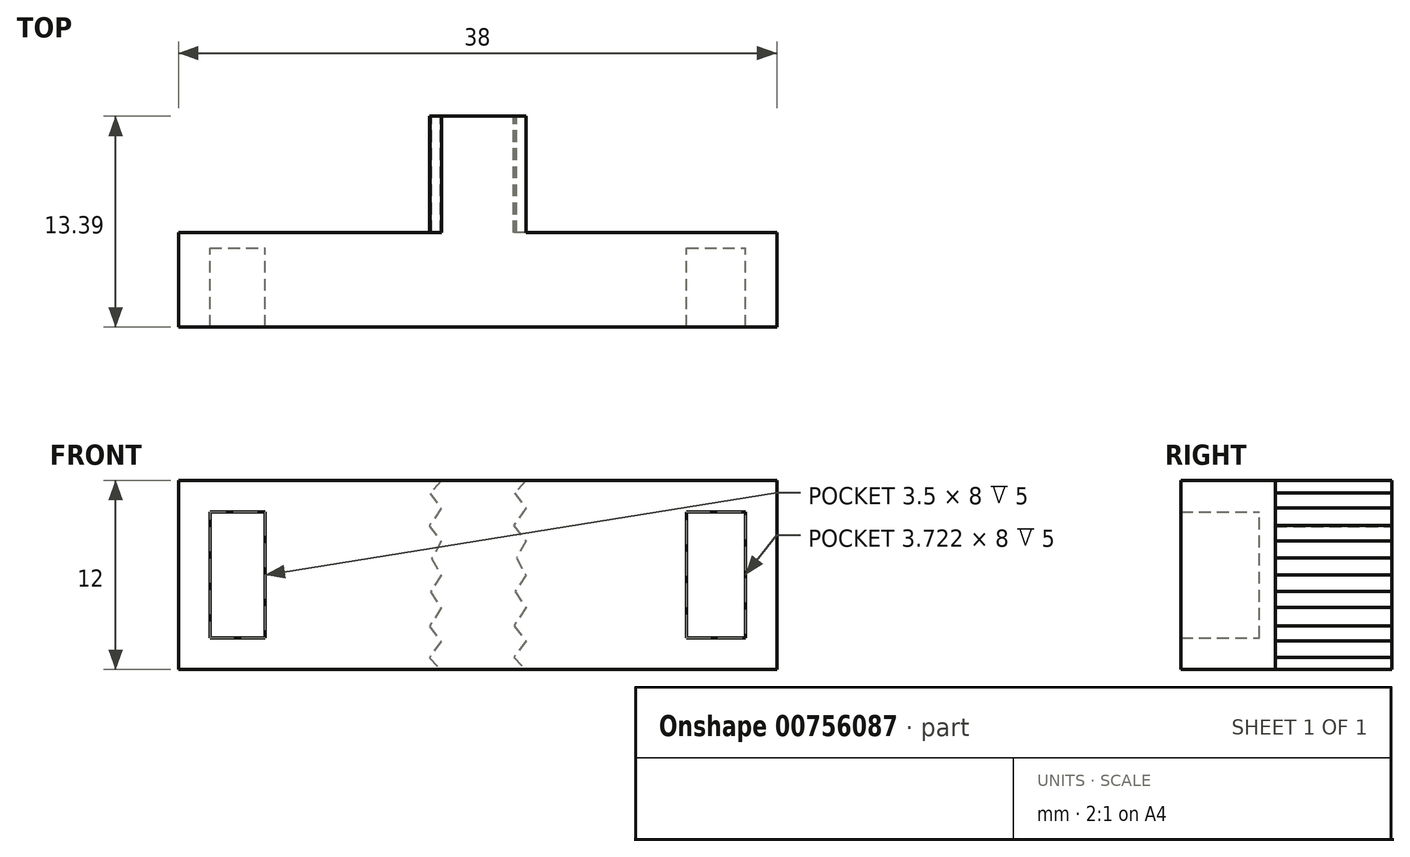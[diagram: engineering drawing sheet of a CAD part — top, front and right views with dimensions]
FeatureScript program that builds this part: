
annotation { "Feature Type Name" : "Feature", "Feature Type Description" : "" }
export const myFeature = defineFeature(function(context is Context, id is Id, definition is map)
    precondition{}
    {
        {
            var Q0;
            Q0=qCreatedBy(makeId("Front.planeOp"),FACE);
            var sketch = newSketch(context, id + "F0", { "sketchPlane" : qUnion([Q0])});
            skLineSegment(sketch, "E0", {"start": v(-23.24, 11.53) * mm, "end": v(10.76, 11.53) * mm});
            skLineSegment(sketch, "E1", {"start": v(-19.74, 17.19) * mm, "end": v(-19.74, 19.53) * mm});
            skLineSegment(sketch, "E2", {"start": v(-19.74, 19.53) * mm, "end": v(7.03, 19.53) * mm});
            skLineSegment(sketch, "E3", {"start": v(7.03, 19.53) * mm, "end": v(7.03, 13.6) * mm});
            skLineSegment(sketch, "E4.bottom", {"start": v(-23.24, 11.53) * mm, "end": v(-19.74, 11.53) * mm});
            skLineSegment(sketch, "E4.top", {"start": v(-23.24, 19.53) * mm, "end": v(-19.74, 19.53) * mm});
            skLineSegment(sketch, "E4.left", {"start": v(-23.24, 11.53) * mm, "end": v(-23.24, 19.53) * mm});
            skLineSegment(sketch, "E4.right", {"start": v(-19.74, 11.53) * mm, "end": v(-19.74, 19.53) * mm});
            skLineSegment(sketch, "E5.bottom", {"start": v(10.76, 11.53) * mm, "end": v(7.03, 11.53) * mm});
            skLineSegment(sketch, "E5.top", {"start": v(10.76, 19.53) * mm, "end": v(7.03, 19.53) * mm});
            skLineSegment(sketch, "E5.left", {"start": v(10.76, 11.53) * mm, "end": v(10.76, 19.53) * mm});
            skLineSegment(sketch, "E5.right", {"start": v(7.03, 11.53) * mm, "end": v(7.03, 19.53) * mm});
            skLineSegment(sketch, "E6.0", {"start": v(12.76, 9.53) * mm, "end": v(12.76, 21.53) * mm});
            skLineSegment(sketch, "E6.1", {"start": v(-19.97, 21.53) * mm, "end": v(7.03, 21.53) * mm});
            skLineSegment(sketch, "E6.2", {"start": v(-25.24, 21.53) * mm, "end": v(-19.97, 21.53) * mm});
            skLineSegment(sketch, "E6.3", {"start": v(12.76, 21.53) * mm, "end": v(7.03, 21.53) * mm});
            skLineSegment(sketch, "E6.4", {"start": v(-25.24, 9.53) * mm, "end": v(-25.24, 21.53) * mm});
            skLineSegment(sketch, "E6.5", {"start": v(-25.24, 9.53) * mm, "end": v(12.76, 9.53) * mm});
            skSolve(sketch);
        }
        {
            var Q0;
            Q0=makeQuery(id+"F0.imprint","IMPRINT",FACE,{"disambiguationData":[TD([[makeQuery(id+"F0.imprint","IMPRINT",EDGE,{"derivedFrom":sQuery(id+"F0.wireOp",EDGE,"E2")}),1.0]])]});
            var Q1;
            Q1=makeQuery(id+"F0.imprint","IMPRINT",FACE,{"disambiguationData":[TD([[makeQuery(id+"F0.imprint","IMPRINT",EDGE,{"derivedFrom":sQuery(id+"F0.wireOp",EDGE,"E1")}),-1.0]])]});
            extrude(context, id + "F1", {"entities" : qUnion([Q0, Q1]), "depth" : 5 * mm, "offsetDistance" : 25.4 * mm});
        }
        {
            var Q0;
            Q0=makeQuery(id+"F0.imprint","IMPRINT",FACE,{"disambiguationData":[TD([[makeQuery(id+"F0.imprint","IMPRINT",EDGE,{"derivedFrom":sQuery(id+"F0.wireOp",EDGE,"E1")}),-1.0]])]});
            var Q1;
            Q1=makeQuery(id+"F0.imprint","IMPRINT",FACE,{"disambiguationData":[TD([[makeQuery(id+"F0.imprint","IMPRINT",EDGE,{"derivedFrom":sQuery(id+"F0.wireOp",EDGE,"E2")}),1.0]])]});
            var Q2;
            Q2=makeQuery(id+"F0.imprint","IMPRINT",FACE,{"disambiguationData":[TD([[makeQuery(id+"F0.imprint","IMPRINT",EDGE,{"derivedFrom":sQuery(id+"F0.wireOp",EDGE,"E3")}),1.0]])]});
            var Q3;
            Q3=makeQuery(id+"F0.imprint","IMPRINT",FACE,{"disambiguationData":[TD([[makeQuery(id+"F0.imprint","IMPRINT",EDGE,{"derivedFrom":sQuery(id+"F0.wireOp",EDGE,"E1")}),1.0]])]});
            extrude(context, id + "F2", {"entities" : qUnion([Q0, Q1, Q2, Q3]), "operationType" : NewBodyOperationType.ADD, "oppositeDirection" : true, "depth" : 1 * mm, "offsetDistance" : 25.4 * mm});
        }
        {
            var Q0;
            Q0=makeQuery(id+"F2.opExtrude","CAP_FACE",FACE,{"disambiguationData":[OSD([sQuery(id+"F0.wireOp",EDGE,"E6.0"),sQuery(id+"F0.wireOp",EDGE,"E6.1"),sQuery(id+"F0.wireOp",EDGE,"E6.2"),sQuery(id+"F0.wireOp",EDGE,"E6.3"),sQuery(id+"F0.wireOp",EDGE,"E6.4"),sQuery(id+"F0.wireOp",EDGE,"E6.5")])],"isStart":false});
            var sketch = newSketch(context, id + "F3", { "sketchPlane" : qUnion([Q0])});
            skLineSegment(sketch, "E7.bottom", {"start": v(3.18, 21.53) * mm, "end": v(9.3, 21.53) * mm});
            skLineSegment(sketch, "E7.top", {"start": v(3.18, 9.53) * mm, "end": v(9.3, 9.53) * mm});
            skLineSegment(sketch, "E7.left", {"start": v(3.18, 21.53) * mm, "end": v(3.18, 9.53) * mm});
            skLineSegment(sketch, "E7.right", {"start": v(9.3, 21.53) * mm, "end": v(9.3, 9.53) * mm});
            skLineSegment(sketch, "E8", {"start": v(3.18, 18.12) * mm, "end": v(-12.76, 18.12) * mm});
            skLineSegment(sketch, "E9", {"start": v(9.3, 18.12) * mm, "end": v(25.24, 18.12) * mm});
            skSolve(sketch);
        }
        {
            var Q0;
            {var subQ4=sQuery(id+"F3.wireOp",EDGE,"E7.bottom");Q0=makeQuery(id+"F3.imprint","IMPRINT",FACE,{"disambiguationData":[TD([[makeQuery(id+"F3.imprint","IMPRINT",EDGE,{"derivedFrom":subQ4}),-1.0]])]});}
            extrude(context, id + "F4", {"entities" : qUnion([Q0]), "operationType" : NewBodyOperationType.ADD, "depth" : 7.4 * mm, "offsetDistance" : 25.4 * mm});
        }
        {
            var Q0;
            Q0=makeQuery(id+"F4.opExtrude","CAP_FACE",FACE,{"disambiguationData":[OSD([sQuery(id+"F3.wireOp",EDGE,"E7.bottom"),sQuery(id+"F3.wireOp",EDGE,"E7.top"),sQuery(id+"F3.wireOp",EDGE,"E7.left"),sQuery(id+"F3.wireOp",EDGE,"E7.right")])],"isStart":false});
            var sketch = newSketch(context, id + "F5", { "sketchPlane" : qUnion([Q0])});
            skLineSegment(sketch, "E10", {"start": v(3.18, 21.53) * mm, "end": v(3.89, 20.75) * mm});
            skLineSegment(sketch, "E11", {"start": v(3.89, 20.75) * mm, "end": v(3.18, 19.78) * mm});
            skLineSegment(sketch, "E12", {"start": v(3.18, 19.78) * mm, "end": v(3.95, 18.67) * mm});
            skLineSegment(sketch, "E13", {"start": v(3.95, 18.67) * mm, "end": v(3.18, 17.68) * mm});
            skLineSegment(sketch, "E14", {"start": v(3.18, 17.68) * mm, "end": v(3.78, 16.6) * mm});
            skLineSegment(sketch, "E15", {"start": v(3.78, 16.6) * mm, "end": v(3.18, 15.53) * mm});
            skLineSegment(sketch, "E16", {"start": v(3.18, 15.53) * mm, "end": v(3.87, 14.46) * mm});
            skLineSegment(sketch, "E17", {"start": v(3.87, 14.46) * mm, "end": v(3.18, 13.47) * mm});
            skLineSegment(sketch, "E18", {"start": v(3.18, 13.47) * mm, "end": v(3.93, 12.29) * mm});
            skLineSegment(sketch, "E19", {"start": v(3.93, 12.29) * mm, "end": v(3.18, 11.33) * mm});
            skLineSegment(sketch, "E20", {"start": v(3.18, 11.33) * mm, "end": v(3.93, 10.3) * mm});
            skLineSegment(sketch, "E21", {"start": v(3.93, 10.3) * mm, "end": v(3.18, 9.53) * mm});
            skLineSegment(sketch, "E22", {"start": v(8.55, 21.53) * mm, "end": v(9.26, 20.72) * mm});
            skLineSegment(sketch, "E23", {"start": v(9.26, 20.72) * mm, "end": v(8.56, 19.74) * mm});
            skLineSegment(sketch, "E24", {"start": v(8.56, 19.74) * mm, "end": v(9.33, 18.64) * mm});
            skLineSegment(sketch, "E25", {"start": v(9.33, 18.64) * mm, "end": v(8.56, 17.65) * mm});
            skLineSegment(sketch, "E26", {"start": v(8.56, 17.65) * mm, "end": v(9.16, 16.57) * mm});
            skLineSegment(sketch, "E27", {"start": v(9.16, 16.57) * mm, "end": v(8.56, 15.5) * mm});
            skLineSegment(sketch, "E28", {"start": v(8.56, 15.5) * mm, "end": v(9.24, 14.43) * mm});
            skLineSegment(sketch, "E29", {"start": v(9.24, 14.43) * mm, "end": v(8.56, 13.44) * mm});
            skLineSegment(sketch, "E30", {"start": v(8.56, 13.44) * mm, "end": v(9.3, 12.26) * mm});
            skLineSegment(sketch, "E31", {"start": v(9.3, 12.26) * mm, "end": v(8.56, 11.3) * mm});
            skLineSegment(sketch, "E32", {"start": v(8.56, 11.3) * mm, "end": v(9.3, 10.27) * mm});
            skLineSegment(sketch, "E33", {"start": v(9.3, 10.27) * mm, "end": v(8.56, 9.5) * mm});
            skLineSegment(sketch, "E34", {"start": v(3.18, 21.53) * mm, "end": v(3.18, 9.53) * mm});
            skLineSegment(sketch, "E35", {"start": v(8.55, 21.53) * mm, "end": v(9.3, 21.53) * mm});
            skLineSegment(sketch, "E36", {"start": v(9.3, 21.53) * mm, "end": v(9.3, 9.53) * mm});
            skLineSegment(sketch, "E37", {"start": v(9.3, 9.53) * mm, "end": v(8.56, 9.5) * mm});
            skSolve(sketch);
        }
        {
            var Q0;
            Q0=makeQuery(id+"F5.imprint","IMPRINT",FACE,{"disambiguationData":[TD([[makeQuery(id+"F5.imprint","IMPRINT",EDGE,{"derivedFrom":sQuery(id+"F5.wireOp",EDGE,"E22")}),1.0]])]});
            var Q1;
            {var subQ0=sQuery(id+"F5.wireOp",EDGE,"E26");Q1=makeQuery(id+"F5.imprint","IMPRINT",FACE,{"disambiguationData":[TD([[makeQuery(id+"F5.imprint","IMPRINT",EDGE,{"derivedFrom":subQ0}),1.0]])]});}
            var Q2;
            {var subQ0=sQuery(id+"F5.wireOp",EDGE,"E31");Q2=makeQuery(id+"F5.imprint","IMPRINT",FACE,{"disambiguationData":[TD([[makeQuery(id+"F5.imprint","IMPRINT",EDGE,{"derivedFrom":subQ0}),1.0]])]});}
            var Q3;
            {var subQ1=sQuery(id+"F5.wireOp",EDGE,"E33");var subQ3=makeQuery(id+"F4.opExtrude","CAP_EDGE",EDGE,{"disambiguationData":[OSD([sQuery(id+"F3.wireOp",EDGE,"E7.top")])],"isStart":false});var subQ4=makeQuery(id+"F5.imprint","INTERSECT",VERTEX,{"derivedFrom":[subQ3,subQ1]});Q3=makeQuery(id+"F5.imprint","IMPRINT",FACE,{"disambiguationData":[TD([[makeQuery(id+"F5.imprint","IMPRINT",EDGE,{"disambiguationData":[TD([[subQ4,1.0]])],"derivedFrom":subQ1}),1.0]])]});}
            var Q4;
            {var subQ0=sQuery(id+"F5.wireOp",EDGE,"E20");Q4=makeQuery(id+"F5.imprint","IMPRINT",FACE,{"disambiguationData":[TD([[makeQuery(id+"F5.imprint","IMPRINT",EDGE,{"derivedFrom":subQ0}),-1.0]])]});}
            var Q5;
            {var subQ0=sQuery(id+"F5.wireOp",EDGE,"E18");Q5=makeQuery(id+"F5.imprint","IMPRINT",FACE,{"disambiguationData":[TD([[makeQuery(id+"F5.imprint","IMPRINT",EDGE,{"derivedFrom":subQ0}),-1.0]])]});}
            var Q6;
            {var subQ0=sQuery(id+"F5.wireOp",EDGE,"E16");Q6=makeQuery(id+"F5.imprint","IMPRINT",FACE,{"disambiguationData":[TD([[makeQuery(id+"F5.imprint","IMPRINT",EDGE,{"derivedFrom":subQ0}),-1.0]])]});}
            var Q7;
            {var subQ0=sQuery(id+"F5.wireOp",EDGE,"E14");Q7=makeQuery(id+"F5.imprint","IMPRINT",FACE,{"disambiguationData":[TD([[makeQuery(id+"F5.imprint","IMPRINT",EDGE,{"derivedFrom":subQ0}),-1.0]])]});}
            var Q8;
            {var subQ0=sQuery(id+"F5.wireOp",EDGE,"E12");Q8=makeQuery(id+"F5.imprint","IMPRINT",FACE,{"disambiguationData":[TD([[makeQuery(id+"F5.imprint","IMPRINT",EDGE,{"derivedFrom":subQ0}),-1.0]])]});}
            var Q9;
            {var subQ0=sQuery(id+"F5.wireOp",EDGE,"E10");Q9=makeQuery(id+"F5.imprint","IMPRINT",FACE,{"disambiguationData":[TD([[makeQuery(id+"F5.imprint","IMPRINT",EDGE,{"derivedFrom":subQ0}),-1.0]])]});}
            extrude(context, id + "F6", {"entities" : qUnion([Q0, Q1, Q2, Q3, Q4, Q5, Q6, Q7, Q8, Q9]), "operationType" : NewBodyOperationType.REMOVE, "oppositeDirection" : true, "depth" : 7.4 * mm, "offsetDistance" : 25.4 * mm});
        }
    });
